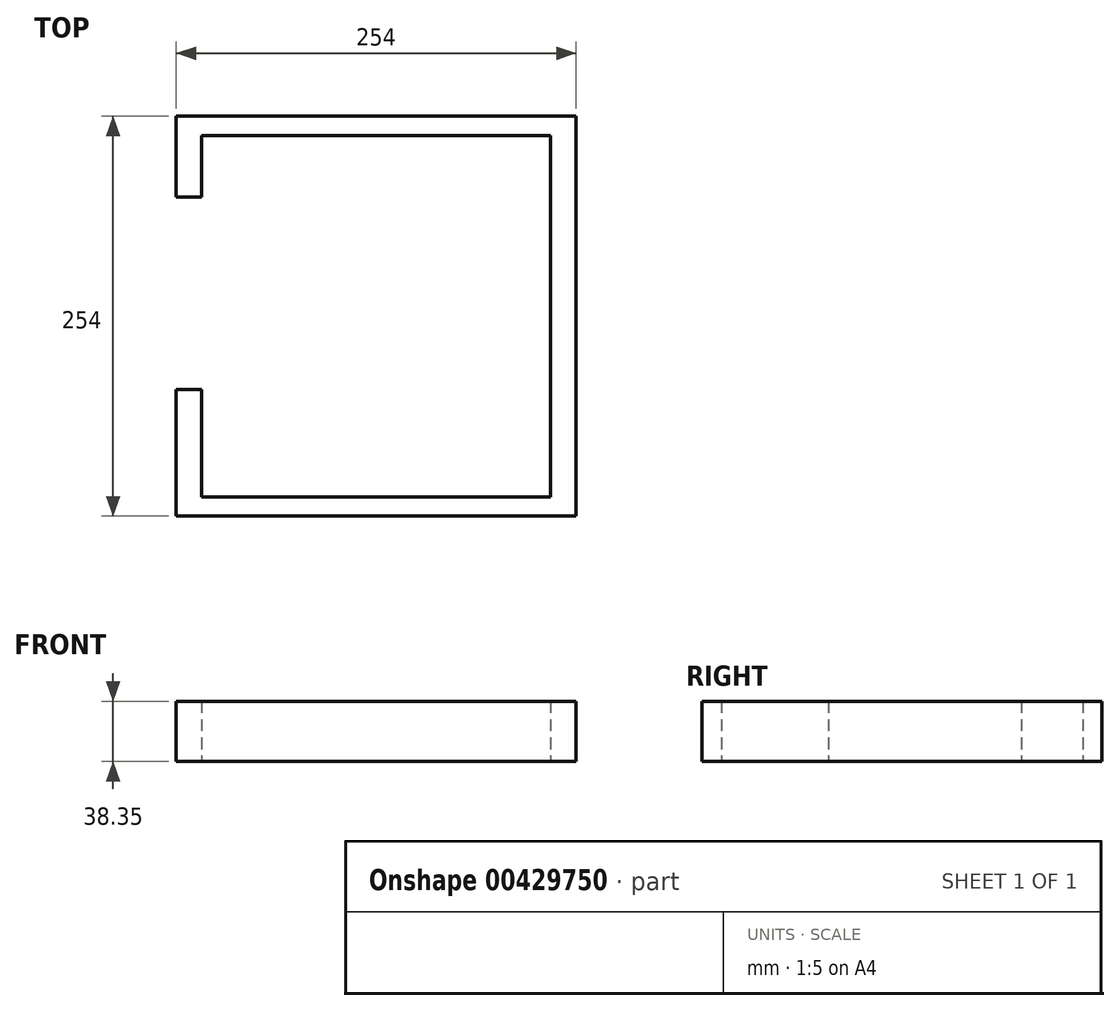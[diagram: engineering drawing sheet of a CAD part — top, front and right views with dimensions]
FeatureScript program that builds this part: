
annotation { "Feature Type Name" : "Feature", "Feature Type Description" : "" }
export const myFeature = defineFeature(function(context is Context, id is Id, definition is map)
    precondition{}
    {
        {
            var Q0;
            Q0=qCreatedBy(makeId("Top.planeOp"),FACE);
            var sketch = newSketch(context, id + "F0", { "sketchPlane" : qUnion([Q0])});
            skLineSegment(sketch, "E0.bottom", {"start": v(127, 127) * mm, "end": v(-127, 127) * mm});
            skLineSegment(sketch, "E0.top", {"start": v(127, -127) * mm, "end": v(-127, -127) * mm});
            skLineSegment(sketch, "E0.left", {"start": v(127, 127) * mm, "end": v(127, -127) * mm});
            skLineSegment(sketch, "E0.right", {"start": v(-127, 127) * mm, "end": v(-127, -127) * mm});
            skPoint(sketch, "E0.middle", {"position": v(0, 0) * mm});
            skLineSegment(sketch, "E1.bottom", {"start": v(110.76, 114.73) * mm, "end": v(-110.76, 114.73) * mm});
            skLineSegment(sketch, "E1.top", {"start": v(110.76, -114.73) * mm, "end": v(-110.76, -114.73) * mm});
            skLineSegment(sketch, "E1.left", {"start": v(110.76, 114.73) * mm, "end": v(110.76, -114.73) * mm});
            skLineSegment(sketch, "E1.right", {"start": v(-110.76, 114.73) * mm, "end": v(-110.76, -114.73) * mm});
            skLineSegment(sketch, "E2.bottom", {"start": v(-127, 75.79) * mm, "end": v(-110.76, 75.79) * mm});
            skLineSegment(sketch, "E2.top", {"start": v(-127, -46.64) * mm, "end": v(-110.76, -46.64) * mm});
            skLineSegment(sketch, "E2.left", {"start": v(-127, 75.79) * mm, "end": v(-127, -46.64) * mm});
            skLineSegment(sketch, "E2.right", {"start": v(-110.76, 75.79) * mm, "end": v(-110.76, -46.64) * mm});
            skLineSegment(sketch, "E3", {"start": v(-110.76, -46.64) * mm, "end": v(-38.05, -114.73) * mm});
            skLineSegment(sketch, "E4", {"start": v(-110.76, 75.79) * mm, "end": v(-38.05, 114.73) * mm});
            skLineSegment(sketch, "E5", {"start": v(110.76, 75.79) * mm, "end": v(36.2, 114.73) * mm});
            skLineSegment(sketch, "E6", {"start": v(110.76, -46.64) * mm, "end": v(36.2, -114.73) * mm});
            skSolve(sketch);
        }
        {
            var Q0;
            Q0=makeQuery(id+"F0.imprint","IMPRINT",FACE,{"disambiguationData":[TD([[makeQuery(id+"F0.imprint","IMPRINT",EDGE,{"derivedFrom":sQuery(id+"F0.wireOp",EDGE,"E0.bottom")}),1.0]])]});
            extrude(context, id + "F1", {"entities" : qUnion([Q0]), "depth" : 38.35 * mm});
        }
    });
